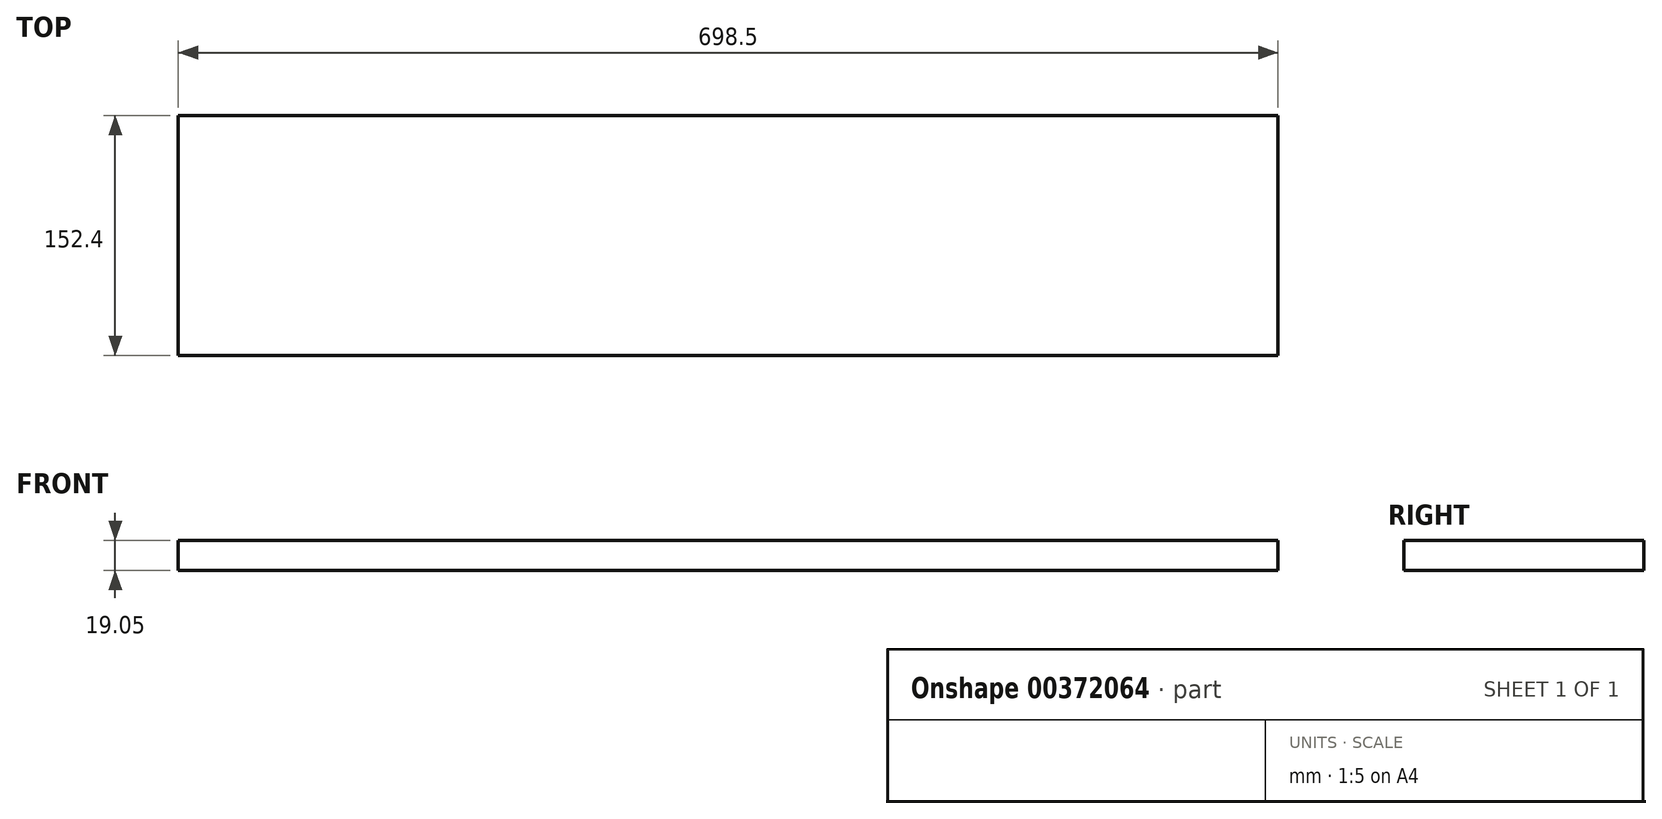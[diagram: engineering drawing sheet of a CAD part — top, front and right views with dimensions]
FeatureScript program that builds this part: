
annotation { "Feature Type Name" : "Feature", "Feature Type Description" : "" }
export const myFeature = defineFeature(function(context is Context, id is Id, definition is map)
    precondition{}
    {
        {
            var Q0;
            Q0=qCreatedBy(makeId("Top.planeOp"),FACE);
            var sketch = newSketch(context, id + "F0", { "sketchPlane" : qUnion([Q0])});
            skLineSegment(sketch, "E0.bottom", {"start": v(0, 0) * mm, "end": v(698.5, 0) * mm});
            skLineSegment(sketch, "E0.top", {"start": v(0, 152.4) * mm, "end": v(698.5, 152.4) * mm});
            skLineSegment(sketch, "E0.left", {"start": v(0, 0) * mm, "end": v(0, 152.4) * mm});
            skLineSegment(sketch, "E0.right", {"start": v(698.5, 0) * mm, "end": v(698.5, 152.4) * mm});
            skSolve(sketch);
        }
        {
            var Q0;
            Q0=makeQuery(id+"F0.imprint","IMPRINT",FACE,{"disambiguationData":[TD([[makeQuery(id+"F0.imprint","IMPRINT",EDGE,{"derivedFrom":sQuery(id+"F0.wireOp",EDGE,"E0.bottom")}),1.0]])]});
            extrude(context, id + "F1", {"entities" : qUnion([Q0]), "depth" : 19.05 * mm});
        }
    });
